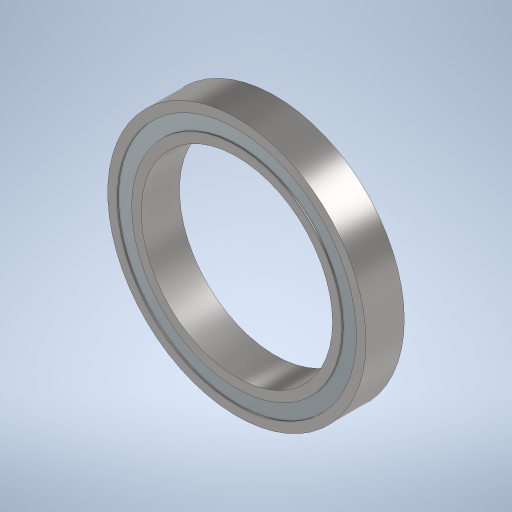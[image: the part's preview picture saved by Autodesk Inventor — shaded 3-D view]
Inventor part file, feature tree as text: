
AUTODESK INVENTOR PART (.ipt)
format: ipt  version: 2024 (Build 280153000, 153)  size: 287,744 bytes
history: native  units: mm
features: extrude x2, sketch x1
ambient origin geometry x8: Origin, YZ Plane, XZ Plane, XY Plane, X Axis, Y Axis, Z Axis, Center Point
bodies: Solid1 (feature_tree)
feature tree (3):
  sketch  "Sketch1"  dims[d0=20.0mm d1=27.0mm d2=1.0mm d3=1.0mm d4=4.0mm d5=0.0mm d6=3.75mm d7=0.0mm]
  extrude  "Extrusion1"  Depth=3.75mm
  extrude  "Extrusion2"  Depth=3.75mm
